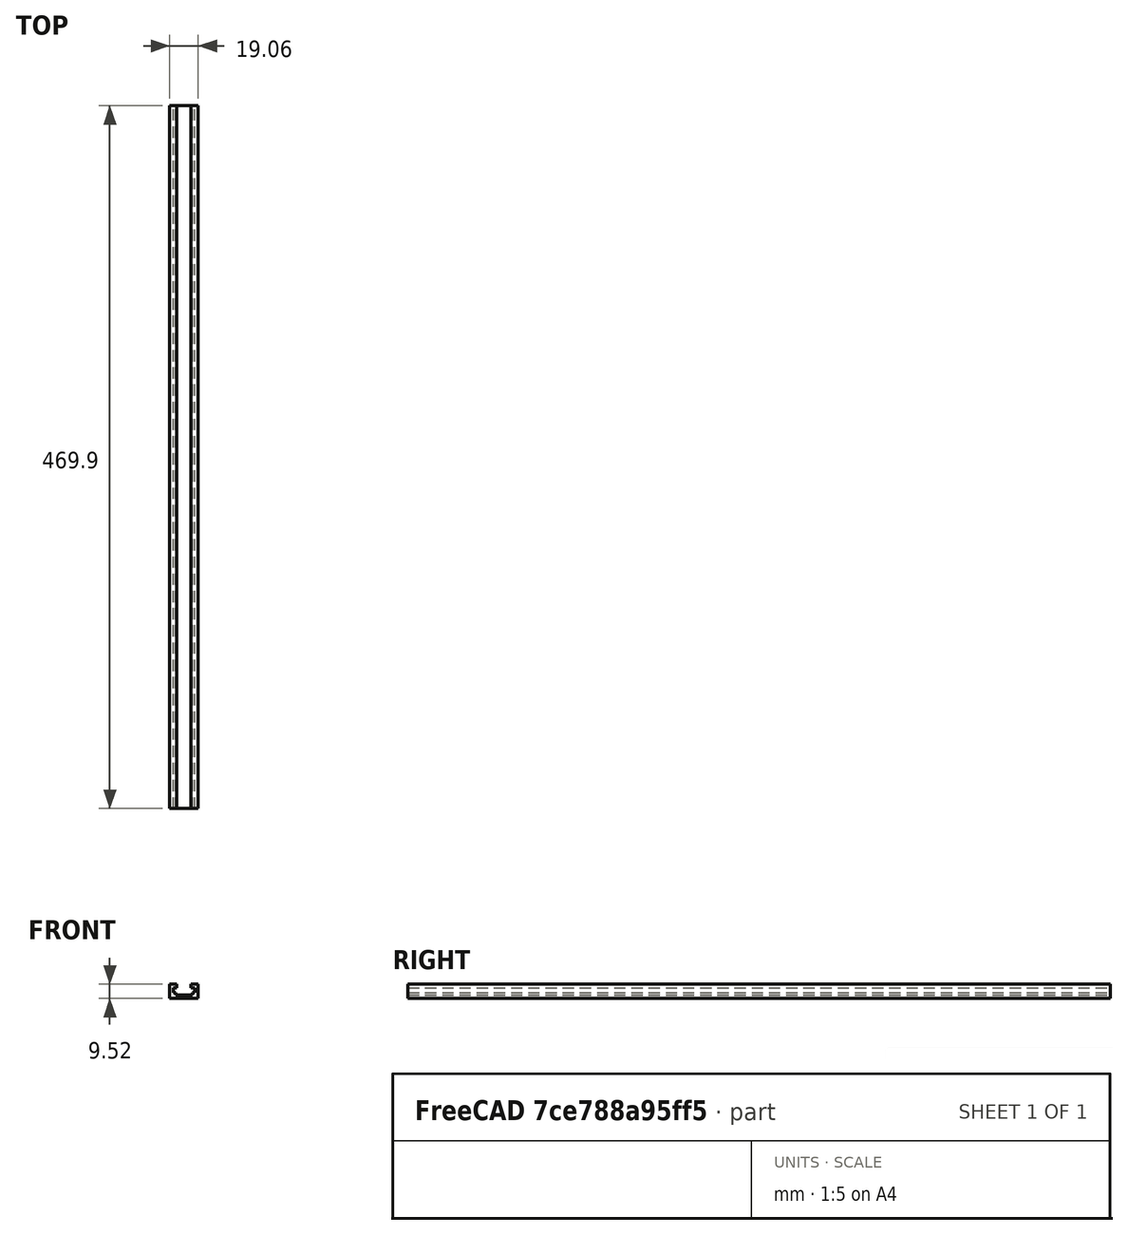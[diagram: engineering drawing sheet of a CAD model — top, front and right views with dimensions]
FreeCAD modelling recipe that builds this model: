
FCSTD DOCUMENT  (FreeCAD 0.20R29603 (Git))
Label: base_t_track
License: All rights reserved
LicenseURL: http://en.wikipedia.org/wiki/All_rights_reserved
objects: Sketcher::SketchObject×4, PartDesign::Pocket×3, TechDraw::DrawProjGroupItem×2, PartDesign::Pad×1, PartDesign::Body×1, TechDraw::DrawSVGTemplate×1, TechDraw::DrawProjGroup×1, TechDraw::DrawViewDimension×1, TechDraw::DrawPage×1
note: 13 computed .brp shape members not serialized (recipe doc carries the construction recipe); baked Part::Feature solids carry a one-line shape summary decoded from their .brp

FEATURE [Sketcher::SketchObject] Sketch
  FullyConstrained = true
  MapMode = 5
  Placement = pos=(0,0,0) rot=(1,0,0;1.5708rad)
  Support = -> [XZ_Plane]
  sketch-geometry (5):
    g0: LineSegment StartX=-9.525 StartY=-4.7625 StartZ=0 EndX=-9.525 EndY=4.7625 EndZ=0
    g1: LineSegment StartX=-9.525 StartY=4.7625 StartZ=0 EndX=9.525 EndY=4.7625 EndZ=0
    g2: LineSegment StartX=9.525 StartY=4.7625 StartZ=0 EndX=9.525 EndY=-4.7625 EndZ=0
    g3: LineSegment StartX=9.525 StartY=-4.7625 StartZ=0 EndX=-9.525 EndY=-4.7625 EndZ=0
    g4: GeomPoint X=0 Y=0 Z=0
  constraints (12):
    c: Coincident(g0,g1)
    c: Coincident(g1,g2)
    c: Coincident(g2,g3)
    c: Coincident(g3,g0)
    c: Horizontal(g1)
    c: Horizontal(g3)
    c: Vertical(g0)
    c: Vertical(g2)
    c: Symmetric(g1,g0,g4)
    c: DistanceX(g1,g1) = 19.05
    c: DistanceY(g2,g2) = 9.525
    c: Coincident(g-1,g4)
FEATURE [PartDesign::Pad] Pad
  Direction = (0,-1,-2e-16)
  Length = 469.9
  Length2 = 10
  Placement = pos=(0,0,0) rot=(1,0,0;1.5708rad)
  Profile = -> Sketch
  ReferenceAxis = -> Sketch [N_Axis]
  Type = 0
FEATURE [Sketcher::SketchObject] Sketch001
  ExternalGeometry = -> [Pad]
  FullyConstrained = true
  MapMode = 5
  Placement = pos=(0,-469.9,-1.034e-13) rot=(1,0,0;1.5708rad)
  Support = -> [Pad]
  sketch-geometry (5):
    g0: LineSegment StartX=-4.7625 StartY=2.38125 StartZ=0 EndX=-4.7625 EndY=4.7625 EndZ=0
    g1: LineSegment StartX=-4.7625 StartY=4.7625 StartZ=0 EndX=4.7625 EndY=4.7625 EndZ=0
    g2: LineSegment StartX=4.7625 StartY=4.7625 StartZ=0 EndX=4.7625 EndY=2.38125 EndZ=0
    g3: LineSegment StartX=4.7625 StartY=2.38125 StartZ=0 EndX=-4.7625 EndY=2.38125 EndZ=0
    g4: GeomPoint X=0 Y=3.57187 Z=0
  constraints (12):
    c: Coincident(g0,g1)
    c: Coincident(g1,g2)
    c: Coincident(g2,g3)
    c: Coincident(g3,g0)
    c: Horizontal(g3)
    c: Vertical(g0)
    c: Vertical(g2)
    c: Symmetric(g1,g0,g4)
    c: Tangent(g1,g-3)
    c: DistanceX(g3,g3) = 9.525
    c: Distance(g2,g-4) = 7.14375
    c: PointOnObject(g4,g-2)
FEATURE [PartDesign::Pocket] Pocket
  BaseFeature = -> Pad
  Direction = (0,1,2e-16)
  Length = 5
  Length2 = 5
  Placement = pos=(0,0,0) rot=(1,0,0;1.5708rad)
  Profile = -> Sketch001
  ReferenceAxis = -> Sketch001 [N_Axis]
  Type = 1
FEATURE [Sketcher::SketchObject] Sketch002
  ExternalGeometry = -> [Pocket]
  FullyConstrained = true
  MapMode = 5
  Placement = pos=(0,-469.9,-1.034e-13) rot=(1,0,0;1.5708rad)
  Support = -> [Pocket]
  sketch-geometry (5):
    g0: LineSegment StartX=-7.14375 StartY=2.38125 StartZ=0 EndX=-7.14375 EndY=-0.79375 EndZ=0
    g1: LineSegment StartX=-7.14375 StartY=-0.79375 StartZ=0 EndX=7.14375 EndY=-0.79375 EndZ=0
    g2: LineSegment StartX=7.14375 StartY=-0.79375 StartZ=0 EndX=7.14375 EndY=2.38125 EndZ=0
    g3: LineSegment StartX=7.14375 StartY=2.38125 StartZ=0 EndX=-7.14375 EndY=2.38125 EndZ=0
    g4: GeomPoint X=0 Y=0.79375 Z=0
  constraints (12):
    c: Coincident(g0,g1)
    c: Coincident(g1,g2)
    c: Coincident(g2,g3)
    c: Coincident(g3,g0)
    c: Horizontal(g1)
    c: Vertical(g0)
    c: Vertical(g2)
    c: Symmetric(g1,g0,g4)
    c: Tangent(g3,g-3)
    c: PointOnObject(g4,g-2)
    c: Distance(g0,g-4) = 3.96875
    c: DistanceX(g1,g1) = 14.2875
FEATURE [PartDesign::Pocket] Pocket001
  BaseFeature = -> Pocket
  Direction = (0,1,2e-16)
  Length = 5
  Length2 = 5
  Placement = pos=(0,0,0) rot=(1,0,0;1.5708rad)
  Profile = -> Sketch002
  ReferenceAxis = -> Sketch002 [N_Axis]
  Type = 1
FEATURE [Sketcher::SketchObject] Sketch003
  ExternalGeometry = -> [Pocket001]
  FullyConstrained = true
  MapMode = 5
  Placement = pos=(0,-469.9,-1.034e-13) rot=(1,0,0;1.5708rad)
  Support = -> [Pocket001]
  sketch-geometry (5):
    g0: LineSegment StartX=-5.55625 StartY=-0.79375 StartZ=0 EndX=-5.55625 EndY=-2.38125 EndZ=0
    g1: LineSegment StartX=-5.55625 StartY=-2.38125 StartZ=0 EndX=5.55625 EndY=-2.38125 EndZ=0
    g2: LineSegment StartX=5.55625 StartY=-2.38125 StartZ=0 EndX=5.55625 EndY=-0.79375 EndZ=0
    g3: LineSegment StartX=5.55625 StartY=-0.79375 StartZ=0 EndX=-5.55625 EndY=-0.79375 EndZ=0
    g4: GeomPoint X=0 Y=-1.5875 Z=0
  constraints (12):
    c: Coincident(g0,g1)
    c: Coincident(g1,g2)
    c: Coincident(g2,g3)
    c: Coincident(g3,g0)
    c: Horizontal(g1)
    c: Vertical(g0)
    c: Vertical(g2)
    c: Symmetric(g1,g0,g4)
    c: DistanceX(g1,g1) = 11.1125
    c: PointOnObject(g4,g-2)
    c: DistanceY(g0,g0) = 1.5875
    c: Tangent(g-3,g3)
FEATURE [PartDesign::Pocket] Pocket002
  BaseFeature = -> Pocket001
  Direction = (0,1,2e-16)
  Length = 5
  Length2 = 5
  Placement = pos=(0,0,0) rot=(1,0,0;1.5708rad)
  Profile = -> Sketch003
  ReferenceAxis = -> Sketch003 [N_Axis]
  Type = 1
FEATURE [PartDesign::Body] Body
  Group = -> [Sketch,Pad,Sketch001,Pocket,Sketch002,Pocket001,Sketch003,Pocket002]
  Origin = -> Origin
  Tip = -> Pocket002
FEATURE [TechDraw::DrawSVGTemplate] Template
  Height = 297
  Orientation = 1
  Width = 420
FEATURE [TechDraw::DrawProjGroupItem] ProjItem  label="Front"
  CoarseView = false
  Direction = (0,0,1)
  Focus = 100
  HardHidden = false
  IsoCount = 0
  IsoHidden = false
  IsoVisible = false
  LockPosition = true
  Perspective = false
  Rotation = 0
  RotationVector = (1,0,0)
  Scale = 0.5
  ScaleType = 2
  SeamHidden = false
  SeamVisible = true
  SmoothHidden = false
  SmoothVisible = true
  Source = -> [Body]
  Type = 0
  X = 0
  XDirection = (1e-16,-1,0)
  Y = 0
FEATURE [TechDraw::DrawProjGroupItem] ProjItem002  label="FrontTopRight"
  CoarseView = false
  Direction = (0.57735,-0.57735,0.57735)
  Focus = 100
  HardHidden = false
  IsoCount = 0
  IsoHidden = false
  IsoVisible = false
  LockPosition = false
  Perspective = false
  Rotation = 0
  RotationVector = (1,0,0)
  Scale = 0.5
  ScaleType = 2
  SeamHidden = false
  SeamVisible = true
  SmoothHidden = false
  SmoothVisible = true
  Source = -> [Body]
  Type = 7
  X = 117.074
  XDirection = (0,-0.707107,-0.707107)
  Y = 97.7244
FEATURE [TechDraw::DrawProjGroup] ProjGroup
  Anchor = -> ProjItem
  AutoDistribute = false
  LockPosition = false
  ProjectionType = 0
  Rotation = 0
  Scale = 0.5
  ScaleType = 2
  Source = -> [Body]
  Views = -> [ProjItem,ProjItem002]
  X = 192.404
  Y = 119.169
  spacingX = 15.0812
  spacingY = 15.0812
FEATURE [TechDraw::DrawViewDimension] Dimension
  AngleOverride = false
  Arbitrary = false
  ArbitraryTolerances = false
  EqualTolerance = true
  ExtensionAngle = 0
  FormatSpec = %.2w
  FormatSpecOverTolerance = %+.2w
  FormatSpecUnderTolerance = %+.2w
  Inverted = false
  LineAngle = 0
  LockPosition = false
  MeasureType = 1
  OverTolerance = 0
  References2D = -> [ProjItem]
  Rotation = 0
  Scale = 0.3
  ScaleType = 0
  TheoreticalExact = false
  Type = 1
  UnderTolerance = 0
  X = 1.4539
  Y = 18.9734
FEATURE [TechDraw::DrawPage] Page
  KeepUpdated = true
  NextBalloonIndex = 1
  ProjectionType = 0
  Scale = 0.3
  Template = -> Template
  Views = -> [ProjGroup,Dimension]
